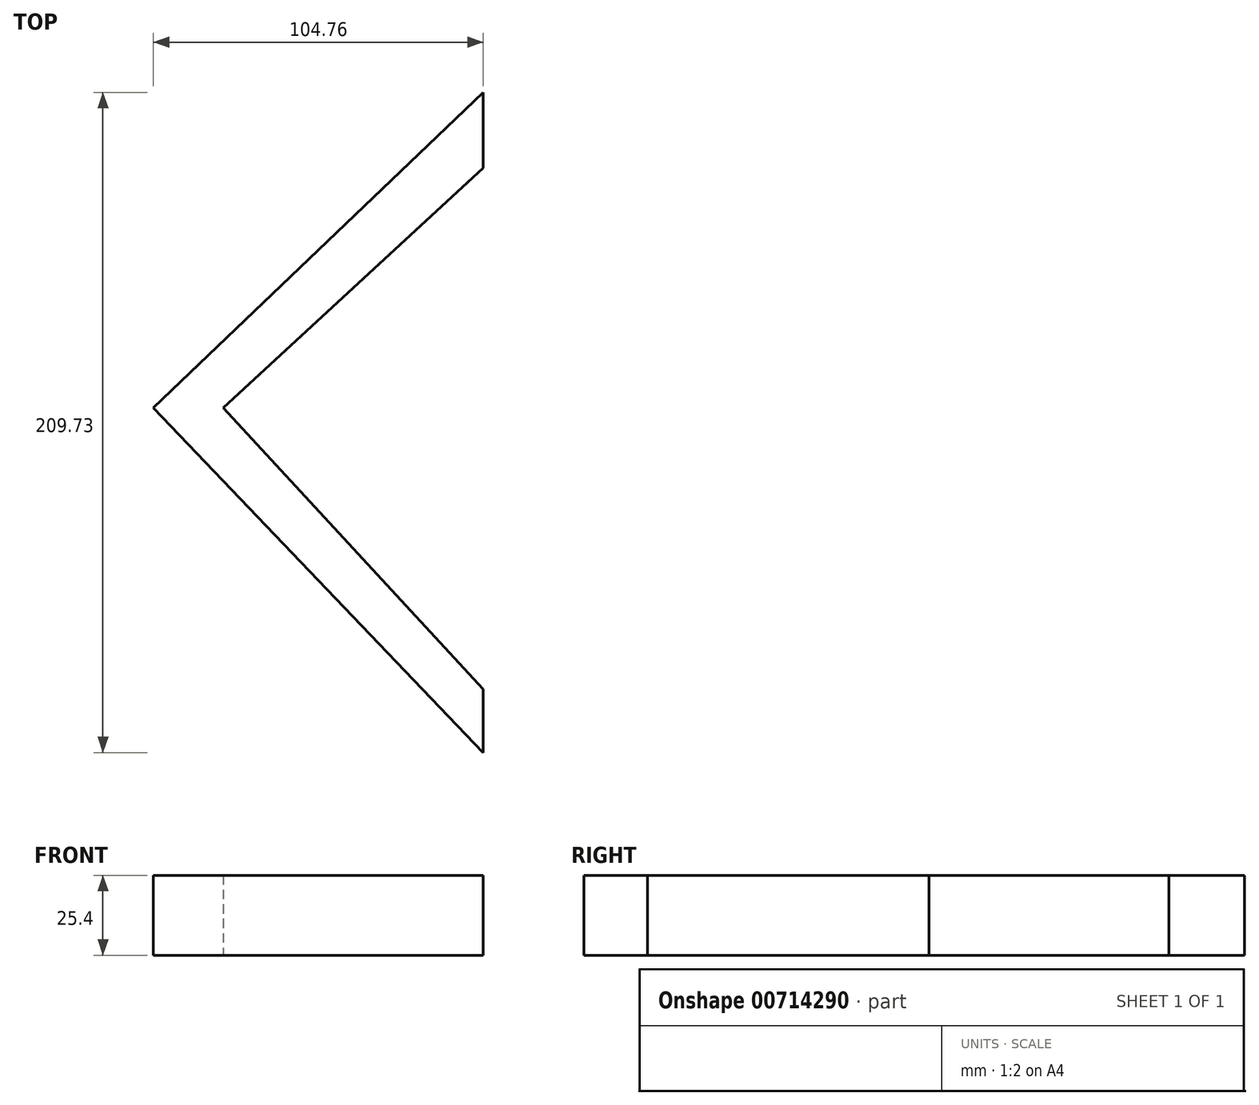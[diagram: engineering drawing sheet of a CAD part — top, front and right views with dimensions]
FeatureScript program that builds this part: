
annotation { "Feature Type Name" : "Feature", "Feature Type Description" : "" }
export const myFeature = defineFeature(function(context is Context, id is Id, definition is map)
    precondition{}
    {
        {
            var Q0;
            Q0=qCreatedBy(makeId("Top.planeOp"),FACE);
            var sketch = newSketch(context, id + "F0", { "sketchPlane" : qUnion([Q0])});
            skLineSegment(sketch, "E0", {"start": v(0, -89.43) * mm, "end": v(-82.55, 0) * mm});
            skLineSegment(sketch, "E1", {"start": v(-82.55, 0) * mm, "end": v(0, 76.2) * mm});
            skLineSegment(sketch, "E2", {"start": v(0, 76.2) * mm, "end": v(0, 100.14) * mm});
            skLineSegment(sketch, "E3", {"start": v(0, 100.14) * mm, "end": v(-104.76, 0) * mm});
            skLineSegment(sketch, "E4", {"start": v(-104.76, 0) * mm, "end": v(0, -109.59) * mm});
            skLineSegment(sketch, "E5", {"start": v(0, -109.59) * mm, "end": v(0, -89.43) * mm});
            skSolve(sketch);
        }
        {
            var Q0;
            Q0 = qSketchRegion(id + "F0", true);
            extrude(context, id + "F1", {"entities" : qUnion([Q0]), "depth" : 25.4 * mm, "offsetDistance" : 25.4 * mm});
        }
    });
